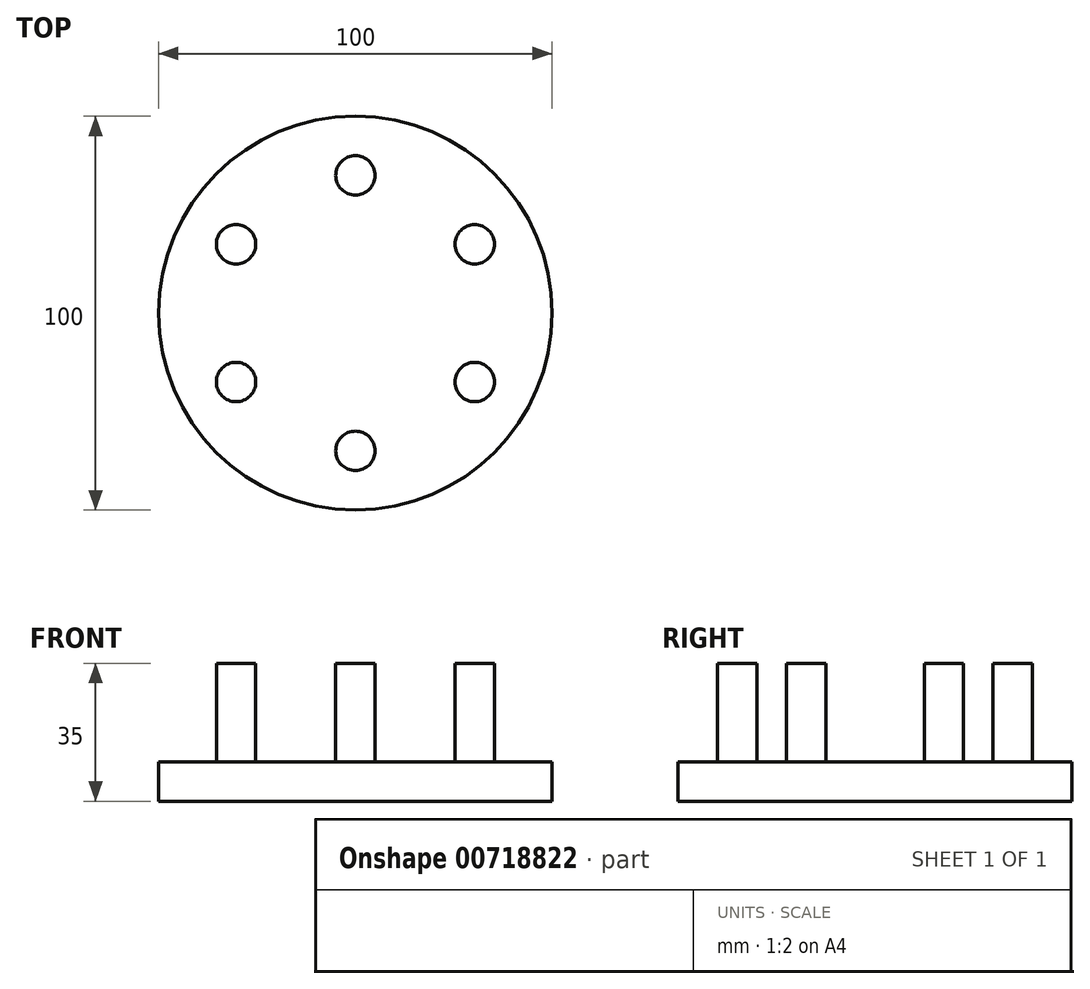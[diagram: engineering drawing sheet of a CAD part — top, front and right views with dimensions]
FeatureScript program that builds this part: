
annotation { "Feature Type Name" : "Feature", "Feature Type Description" : "" }
export const myFeature = defineFeature(function(context is Context, id is Id, definition is map)
    precondition{}
    {
        {
            var Q0;
            Q0=qCreatedBy(makeId("Top.planeOp"),FACE);
            var sketch = newSketch(context, id + "F0", { "sketchPlane" : qUnion([Q0])});
            skCircle(sketch, "E0", {"center": v(0, 0) * mm, "radius": 50 * mm});
            skSolve(sketch);
        }
        {
            var Q0;
            Q0 = qSketchRegion(id + "F0", true);
            extrude(context, id + "F1", {"entities" : qUnion([Q0]), "endBound" : BoundingType.SYMMETRIC, "depth" : 10 * mm, "offsetDistance" : 25 * mm});
        }
        {
            var Q0;
            Q0=makeQuery(id+"F1.opExtrude","CAP_FACE",FACE,{"disambiguationData":[OSD([sQuery(id+"F0.wireOp",EDGE,"E0")])],"isStart":false});
            var sketch = newSketch(context, id + "F2", { "sketchPlane" : qUnion([Q0])});
            skCircle(sketch, "E1", {"center": v(0, 35) * mm, "radius": 5 * mm});
            skPoint(sketch, "E2.center", {"position": v(0, 0) * mm});
            skLineSegment(sketch, "E2.anchor1", {"start": v(0, 0) * mm, "end": v(0, 35) * mm, "construction": true});
            skLineSegment(sketch, "E2.anchor2", {"start": v(0, 0) * mm, "end": v(0, 35) * mm, "construction": true});
            skCircle(sketch, "E3.1.0", {"center": v(-30.31, 17.5) * mm, "radius": 5 * mm});
            skCircle(sketch, "E3.2.0", {"center": v(-30.31, -17.5) * mm, "radius": 5 * mm});
            skCircle(sketch, "E4.1.3.0", {"center": v(0, -35) * mm, "radius": 5 * mm});
            skCircle(sketch, "E4.1.4.0", {"center": v(30.31, -17.5) * mm, "radius": 5 * mm});
            skCircle(sketch, "E4.1.5.0", {"center": v(30.31, 17.5) * mm, "radius": 5 * mm});
            skSolve(sketch);
        }
        {
            var Q0;
            Q0 = qSketchRegion(id + "F2", true);
            extrude(context, id + "F3", {"entities" : qUnion([Q0]), "operationType" : NewBodyOperationType.ADD, "depth" : 25 * mm, "offsetDistance" : 25 * mm});
        }
    });
